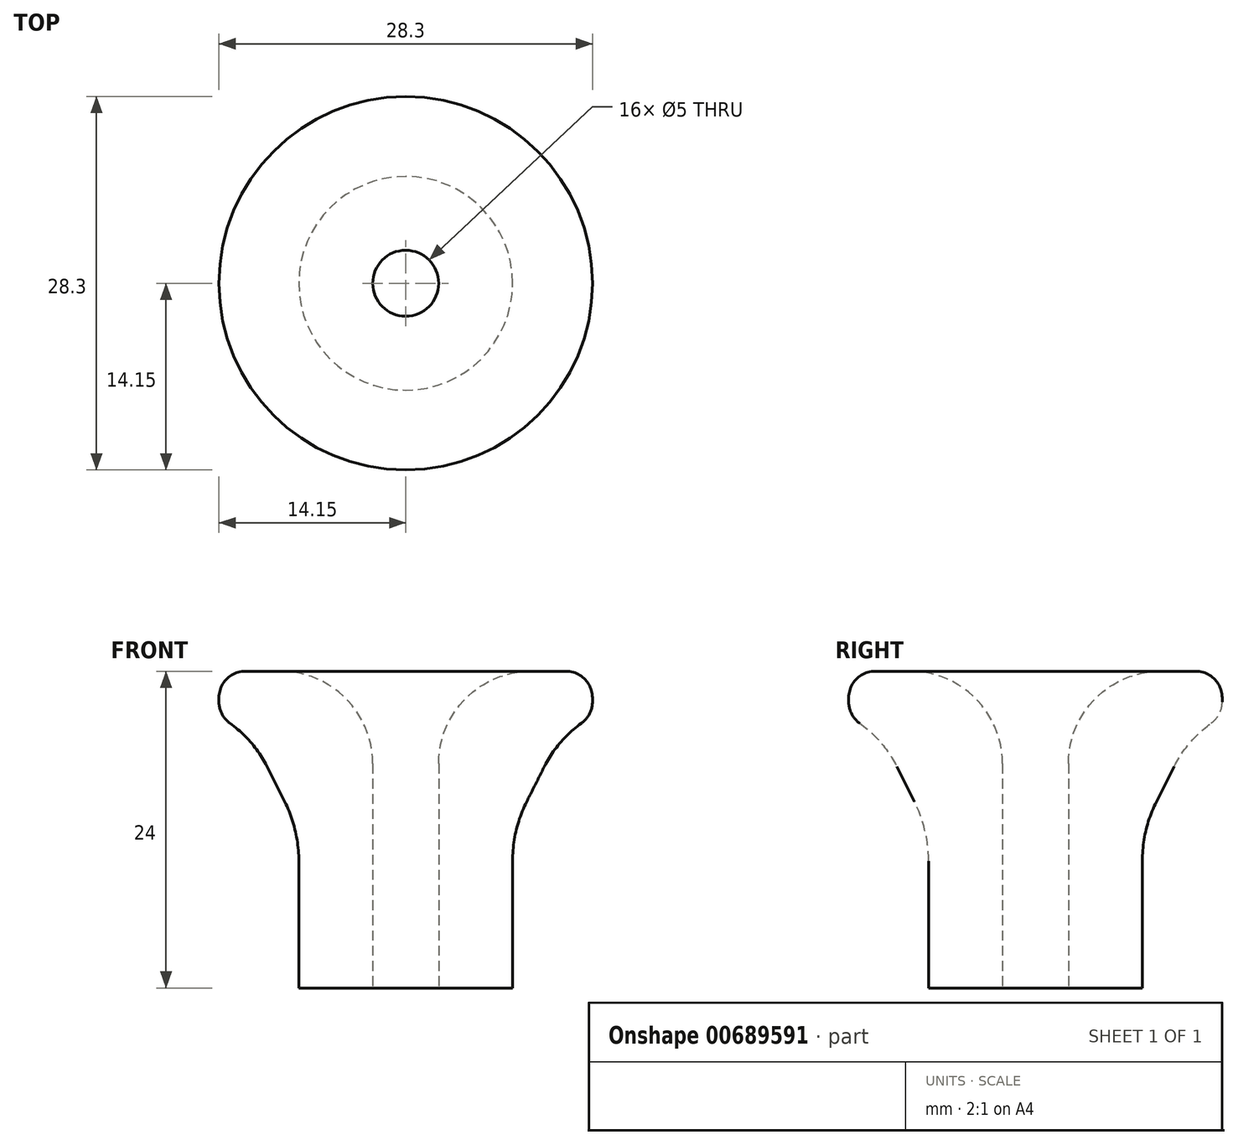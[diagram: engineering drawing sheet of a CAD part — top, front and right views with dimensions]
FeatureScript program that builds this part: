
annotation { "Feature Type Name" : "Feature", "Feature Type Description" : "" }
export const myFeature = defineFeature(function(context is Context, id is Id, definition is map)
    precondition{}
    {
        {
            var Q0;
            Q0=qCreatedBy(makeId("Front.planeOp"),FACE);
            var sketch = newSketch(context, id + "F0", { "sketchPlane" : qUnion([Q0])});
            skLineSegment(sketch, "E0", {"start": v(0, 0) * mm, "end": v(0, 24) * mm});
            skLineSegment(sketch, "E1", {"start": v(0, 0) * mm, "end": v(8.1, 0) * mm});
            skLineSegment(sketch, "E2", {"start": v(0, 24) * mm, "end": v(14.15, 24) * mm});
            skLineSegment(sketch, "E3", {"start": v(8.1, 0) * mm, "end": v(8.1, 12) * mm});
            skLineSegment(sketch, "E4", {"start": v(8.1, 12) * mm, "end": v(11.97, 19.68) * mm});
            skLineSegment(sketch, "E5", {"start": v(11.97, 19.68) * mm, "end": v(14.15, 19.68) * mm});
            skLineSegment(sketch, "E6", {"start": v(14.15, 24) * mm, "end": v(14.15, 19.68) * mm});
            skSolve(sketch);
        }
        {
            var Q0;
            Q0 = qSketchRegion(id + "F0", true);
            var Q1;
            Q1=sQuery(id+"F0.wireOp",EDGE,"E0");
            revolve(context, id + "F1", {"entities" : qUnion([Q0]), "axis" : qUnion([Q1]), "revolveType" : RevolveType.FULL});
        }
        {
            var Q0;
            Q0=makeQuery(id+"F1.opRevolve","SWEPT_FACE",FACE,{"disambiguationData":[OSD([sQuery(id+"F0.wireOp",EDGE,"E1")])]});
            var sketch = newSketch(context, id + "F2", { "sketchPlane" : qUnion([Q0])});
            skCircle(sketch, "E7", {"center": v(0, 0) * mm, "radius": 2.5 * mm});
            skSolve(sketch);
        }
        {
            var Q0;
            Q0 = qSketchRegion(id + "F2", true);
            extrude(context, id + "F3", {"entities" : qUnion([Q0]), "operationType" : NewBodyOperationType.REMOVE, "oppositeDirection" : true, "depth" : 25 * mm, "offsetDistance" : 25 * mm});
        }
        {
            var Q0;
            Q0=makeQuery(id+"F1.opRevolve","SWEPT_EDGE",EDGE,{"disambiguationData":[OSD([sQuery(id+"F0.wireOp",EDGE,"E2"),sQuery(id+"F0.wireOp",EDGE,"E6")])]});
            var Q1;
            Q1=makeQuery(id+"F1.opRevolve","SWEPT_EDGE",EDGE,{"disambiguationData":[OSD([sQuery(id+"F0.wireOp",EDGE,"E5"),sQuery(id+"F0.wireOp",EDGE,"E6")])]});
            fillet(context, id + "F4", {"entities" : qUnion([Q0, Q1]), "radius" : 2 * mm, "tangentPropagation" : true, "allowEdgeOverflow" : false});
        }
        {
            var Q0;
            Q0=makeQuery(id+"F1.opRevolve","SWEPT_EDGE",EDGE,{"disambiguationData":[OSD([sQuery(id+"F0.wireOp",EDGE,"E4"),sQuery(id+"F0.wireOp",EDGE,"E5")])]});
            fillet(context, id + "F5", {"entities" : qUnion([Q0]), "radius" : 9 * mm, "tangentPropagation" : true, "allowEdgeOverflow" : false});
        }
        {
            var Q0;
            Q0=makeQuery(id+"F1.opRevolve","SWEPT_EDGE",EDGE,{"disambiguationData":[OSD([sQuery(id+"F0.wireOp",EDGE,"E3"),sQuery(id+"F0.wireOp",EDGE,"E4")])]});
            fillet(context, id + "F6", {"entities" : qUnion([Q0]), "radius" : 10 * mm, "tangentPropagation" : true, "allowEdgeOverflow" : false});
        }
        {
            var Q0;
            Q0=makeQuery(id+"F3.boolean.opBoolean","INTERSECT",EDGE,{"derivedFrom":[makeQuery(id+"F1.opRevolve","SWEPT_FACE",FACE,{"disambiguationData":[OSD([sQuery(id+"F0.wireOp",EDGE,"E2")])]}),makeQuery(id+"F3.opExtrude","SWEPT_FACE",FACE,{"disambiguationData":[OSD([sQuery(id+"F2.wireOp",EDGE,"E7")])]})]});
            fillet(context, id + "F7", {"entities" : qUnion([Q0]), "radius" : 7 * mm, "tangentPropagation" : true, "allowEdgeOverflow" : false});
        }
    });
